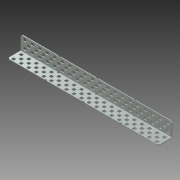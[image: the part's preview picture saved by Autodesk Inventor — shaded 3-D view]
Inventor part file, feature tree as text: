
AUTODESK INVENTOR PART (.ipt)
format: ipt  version: 2013 (Build 170138000, 138)  size: 1,454,592 bytes
history: native  units: in
note: dims shown in document units (in); Inventor stores cm internally (conversion verified against a paired STEP export)
features: other x127, extrude x118, sketch x10, pattern_linear x7, sheet_metal_op x4, projected_geometry x2, plane x1, mirror x1
ambient origin geometry x8: Origin, YZ Plane, XZ Plane, XY Plane, X Axis, Y Axis, Z Axis, Center Point
bodies: Solid1 (feature_tree)
feature tree (270):
  sheet_metal_op  "Face1"
  sheet_metal_op  "Flange1"
  sketch  "Sketch3"  dims[d2=0.032in]
  pattern_linear  "Rectangular Pattern1"  Spacing1=0.032in  [1 undecoded]
  pattern_linear  "Rectangular Pattern2"  Spacing1=0.032in  [1 undecoded]
  pattern_linear  "Rectangular Pattern3"  Spacing1=0.078in  [1 undecoded]
  pattern_linear  "Rectangular Pattern4"  Spacing1=0.182in  [1 undecoded]
  plane  "Work Plane1"
  mirror  "Mirror1"
  other  "Corner Chamfer1"
  pattern_linear  "Rectangular Pattern5"  Spacing1=0.182in  [1 undecoded]
  pattern_linear  "Rectangular Pattern6"  Spacing1=0.113in  [1 undecoded]
  pattern_linear  "Rectangular Pattern7"  Spacing1=0.159in  [1 undecoded]
  sketch  "Sketch1"  dims[d0=10.0in]
  other  "Plate1"
  sketch  "Sketch2"  dims[d1=0.922in]
  other  "Plate2"
  sheet_metal_op  "Bend1"
  sheet_metal_op  "Corner1"
  projected_geometry  "Projected Loop1"
  projected_geometry  "Projected Loop2"
  sketch  "Sketch4"  dims[d3=0.046in]
  sketch  "Sketch5"  dims[d4=0.023in]
  sketch  "Sketch6"  dims[d5=0.092in]
  other  "Srf1"
  other  "Srf2"
  other  "Srf3"
  other  "Srf4"
  other  "Srf5"
  other  "Srf6"
  other  "Srf7"
  other  "Srf8"
  other  "Srf9"
  other  "Srf10"
  other  "Srf11"
  other  "Srf12"
  other  "Srf13"
  other  "Srf14"
  other  "Srf15"
  other  "Srf16"
  other  "Srf17"
  other  "Srf18"
  other  "Srf19"
  other  "Srf20"
  other  "Srf21"
  other  "Srf22"
  other  "Srf23"
  other  "Srf24"
  other  "Srf25"
  other  "Srf26"
  other  "Srf27"
  other  "Srf28"
  other  "Srf29"
  other  "Srf30"
  other  "Srf31"
  other  "Srf32"
  other  "Srf33"
  other  "Srf34"
  other  "Srf35"
  other  "Srf36"
  other  "Srf37"
  other  "Srf38"
  other  "Srf39"
  other  "Srf40"
  sketch  "Sketch7"  dims[d6=0.032in]
  other  "Srf401"
  other  "Srf402"
  other  "Srf403"
  other  "Srf404"
  other  "Srf405"
  other  "Srf406"
  other  "Srf407"
  other  "Srf408"
  other  "Srf409"
  other  "Srf410"
  other  "Srf411"
  other  "Srf412"
  other  "Srf413"
  other  "Srf414"
  other  "Srf415"
  other  "Srf416"
  other  "Srf417"
  other  "Srf418"
  other  "Srf419"
  other  "Work Axis1"
  other  "Srf439"
  other  "Srf440"
  other  "Srf441"
  other  "Srf442"
  other  "Srf443"
  other  "Srf444"
  other  "Srf445"
  other  "Srf446"
  other  "Srf447"
  other  "Srf448"
  other  "Srf449"
  other  "Srf450"
  other  "Srf451"
  other  "Srf452"
  other  "Srf453"
  other  "Srf454"
  other  "Srf455"
  other  "Srf456"
  other  "Srf457"
  other  "Srf458"
  other  "Srf459"
  other  "Srf460"
  other  "Srf461"
  other  "Srf462"
  other  "Srf463"
  other  "Srf464"
  other  "Srf465"
  other  "Srf466"
  other  "Srf467"
  other  "Srf468"
  other  "Srf469"
  other  "Srf470"
  other  "Srf471"
  other  "Srf472"
  other  "Srf473"
  other  "Srf474"
  other  "Srf475"
  other  "Srf476"
  other  "Srf477"
  other  "Srf478"
  other  "Srf420"
  other  "Srf421"
  other  "Srf422"
  other  "Srf423"
  other  "Srf424"
  other  "Srf425"
  other  "Srf426"
  other  "Srf427"
  other  "Srf428"
  other  "Srf429"
  other  "Srf430"
  other  "Srf431"
  other  "Srf432"
  other  "Srf433"
  other  "Srf434"
  other  "Srf435"
  other  "Srf436"
  other  "Srf437"
  other  "Srf438"
  sketch  "Sketch8"  dims[d7=0.922in d8=90.0deg d9=0.032in]
  sketch  "Sketch9"  dims[d10=0.184in]
  sketch  "Sketch10"  dims[d11=0.046in d12=0.032in d13=0.032in d14=0.078in d15=0.182in d16=0.182in d17=0.113in d18=0.159in d19=0.02in d20=0.046in d21=0.0in d22=7.874in d24=0.5in d25=0.7874in d27=0.5in d28=0.182in d29=0.182in d30=0.25in d31=0.25in d32=0.046in d33=0.0in d34=0.02in d35=7.4803in d37=0.5in d38=1.0in d39=0.0in d40=7.874in d42=0.5in d43=0.7874in d45=0.5in d46=1.0in d47=0.0in d48=7.4803in d50=0.5in d51=135.0deg d52=0.0in d53=0.0in d54=0.0in d55=0.0in d56=0.0in d57=0.0in d58=0.0in d59=0.0in d60=0.0in d61=0.0in d62=0.0in d63=0.0in d64=0.0in d65=0.0in d66=0.0in d67=0.0in d68=0.0in d69=0.0in d70=0.0in d71=0.0in d72=0.0in d73=0.0in d74=0.0in d75=0.0in d76=0.0in d77=0.0in d78=0.0in d79=0.0in d80=0.0in d81=0.0in d82=0.0in d83=0.0in d84=0.0in d85=0.0in d86=0.0in d87=0.0in d88=0.0in d89=0.0in d90=0.0in d91=0.0in d92=0.0in d93=0.0in d94=0.0in d95=0.0in d96=0.0in d97=0.0in d98=0.0in d99=0.0in d100=0.0in d101=0.0in d102=0.0in d103=0.0in d104=0.0in d105=0.0in d106=0.0in d107=0.0in d108=0.0in d109=0.0in d110=0.0in d111=0.0in d112=0.0in d113=0.0in d114=0.0in d115=0.0in d116=0.0in d117=0.0in d118=0.0in d119=0.0in d120=0.0in d121=0.0in d122=0.0in d123=0.0in d124=0.0in d125=0.0in d126=0.0in d127=0.0in d128=0.0in d129=0.0in d130=0.0in d131=0.0in d132=0.0in d133=0.0in d134=0.0in d135=0.0in d136=0.0in d137=0.0in d138=0.0in d139=0.0in d140=0.0in d141=0.0in d142=0.0in d143=0.0in d144=0.0in d145=0.0in d146=0.0in d147=0.0in d148=0.0in d149=0.0in d150=0.0in d151=0.0in d152=0.0in d153=0.0in d154=0.0in d155=0.0in d156=0.0in d157=0.0in d158=0.0in d159=0.0in d160=0.0in d161=0.0in d162=0.0in d163=0.0in d164=0.0in d165=0.0in d166=0.0in d167=0.0in d168=0.0in d169=0.0in d170=0.09in d171=0.25in d172=45.0deg d173=0.16in d174=0.046in d175=0.0in d176=1.1811in d178=2.5in d179=0.16in d180=0.046in d181=0.0in d182=1.1811in d184=2.5in d186=0.078in d190=0.039in d191=0.6508in d192=0.046in d193=0.046in d194=0.0in d195=1.1811in d197=2.5in d198=0.0in d199=0.0in d200=0.0in d201=0.0in d202=0.0in d203=0.0in d204=0.0in d205=0.0in d206=0.0in d207=0.0in d208=0.0in d209=0.0in d210=0.0in d211=0.0in d212=0.0in d213=0.0in d214=0.0in d215=0.0in d216=0.0in d217=0.0in d218=0.0in d219=0.0in d220=0.0in d221=0.0in d222=0.0in d223=0.0in d224=0.0in d225=0.0in d226=0.0in d227=0.0in d228=0.0in d229=0.0in d230=0.0in d231=0.0in d232=0.0in d233=0.0in d234=0.0in d235=0.0in d236=0.0in d237=0.0in d238=0.0in d239=0.0in d240=0.0in d241=0.0in d242=0.0in d243=0.0in d244=0.0in d245=0.0in d246=0.0in d247=0.0in d248=0.0in d249=0.0in d250=0.0in d251=0.0in d252=0.0in d253=0.0in d254=0.0in d255=0.0in d256=0.0in d257=0.0in d258=0.0in d259=0.0in d260=0.0in d261=0.0in d262=0.0in d263=0.0in d264=0.0in d265=0.0in d266=0.0in d267=0.0in d268=0.0in d269=0.0in d270=0.0in d271=0.0in d272=0.0in d273=0.0in d274=0.0in d275=0.0in d276=0.0in d277=0.0in d278=0.0in d279=0.0in d280=0.0in d281=0.0in d282=0.0in d283=0.0in d284=0.0in d285=0.0in d286=0.0in d287=0.0in d288=0.0in d289=0.0in d290=0.0in d291=0.0in d292=0.0in d293=0.0in d294=0.0in d295=0.0in d296=0.0in d297=0.0in d298=0.0in d299=0.0in d300=0.0in d301=0.0in d302=0.0in d303=0.0in d304=0.0in d305=0.0in d306=0.0in d307=0.0in d308=0.0in d309=0.0in d310=0.0in d311=0.0in d312=0.0in d313=0.0in d314=0.0in d315=0.0in]
  other  "Cut1"
  other  "Cut2"
  extrude  "ExtrusionSrf1"  Depth=0.02in
  extrude  "ExtrusionSrf401"  Depth=0.046in
  other  "Cut3"
  other  "Cut4"
  other  "Cut5"
  extrude  "ExtrusionSrf2"  TaperAngle=0.0deg  [1 undecoded]
  extrude  "ExtrusionSrf3"  Depth=7.874in
  extrude  "ExtrusionSrf4"  Depth=0.7874in
  extrude  "ExtrusionSrf5"  Depth=0.182in
  extrude  "ExtrusionSrf6"  Depth=0.182in
  extrude  "ExtrusionSrf7"  Depth=0.25in
  extrude  "ExtrusionSrf8"  Depth=0.25in
  extrude  "ExtrusionSrf9"  Depth=0.046in
  extrude  "ExtrusionSrf10"  TaperAngle=0.0deg  [1 undecoded]
  extrude  "ExtrusionSrf11"  Depth=0.02in
  extrude  "ExtrusionSrf12"  Depth=7.4803in
  extrude  "ExtrusionSrf13"  Depth=1.0in TaperAngle=0.0deg
  extrude  "ExtrusionSrf14"  Depth=7.874in
  extrude  "ExtrusionSrf15"  Depth=1.0in TaperAngle=0.0deg
  extrude  "ExtrusionSrf16"  Depth=7.4803in
  extrude  "ExtrusionSrf17"  TaperAngle=135.0deg  [1 undecoded]
  extrude  "ExtrusionSrf18"  Depth=0.16in
  extrude  "ExtrusionSrf19"  Depth=0.046in
  extrude  "ExtrusionSrf20"  TaperAngle=0.0deg  [1 undecoded]
  extrude  "ExtrusionSrf21"  Depth=1.1811in
  extrude  "ExtrusionSrf22"  Depth=0.16in
  extrude  "ExtrusionSrf23"  Depth=0.046in
  extrude  "ExtrusionSrf24"  TaperAngle=0.0deg  [1 undecoded]
  extrude  "ExtrusionSrf25"  Depth=1.1811in
  extrude  "ExtrusionSrf26"  Depth=0.078in
  extrude  "ExtrusionSrf27"  Depth=0.039in
  extrude  "ExtrusionSrf28"  Depth=0.6508in
  extrude  "ExtrusionSrf29"  Depth=0.046in
  extrude  "ExtrusionSrf30"  Depth=0.046in
  extrude  "ExtrusionSrf31"  TaperAngle=0.0deg  [1 undecoded]
  extrude  "ExtrusionSrf32"  Depth=1.1811in
  extrude  "ExtrusionSrf33"  [1 undecoded]
  extrude  "ExtrusionSrf34"  [1 undecoded]
  extrude  "ExtrusionSrf35"  [1 undecoded]
  extrude  "ExtrusionSrf36"  [1 undecoded]
  extrude  "ExtrusionSrf37"  [1 undecoded]
  extrude  "ExtrusionSrf38"  [1 undecoded]
  extrude  "ExtrusionSrf39"  [1 undecoded]
  extrude  "ExtrusionSrf40"  [1 undecoded]
  extrude  "ExtrusionSrf402"  [1 undecoded]
  extrude  "ExtrusionSrf403"  [1 undecoded]
  extrude  "ExtrusionSrf404"  [1 undecoded]
  extrude  "ExtrusionSrf405"  [1 undecoded]
  extrude  "ExtrusionSrf406"  [1 undecoded]
  extrude  "ExtrusionSrf407"  [1 undecoded]
  extrude  "ExtrusionSrf408"  [1 undecoded]
  extrude  "ExtrusionSrf409"  [1 undecoded]
  extrude  "ExtrusionSrf410"  [1 undecoded]
  extrude  "ExtrusionSrf411"  [1 undecoded]
  extrude  "ExtrusionSrf412"  [1 undecoded]
  extrude  "ExtrusionSrf413"  [1 undecoded]
  extrude  "ExtrusionSrf414"  [1 undecoded]
  extrude  "ExtrusionSrf415"  [1 undecoded]
  extrude  "ExtrusionSrf416"  [1 undecoded]
  extrude  "ExtrusionSrf417"  [1 undecoded]
  extrude  "ExtrusionSrf418"  [1 undecoded]
  extrude  "ExtrusionSrf419"  [1 undecoded]
  extrude  "ExtrusionSrf420"  [1 undecoded]
  extrude  "ExtrusionSrf421"  [1 undecoded]
  extrude  "ExtrusionSrf422"  [1 undecoded]
  extrude  "ExtrusionSrf423"  [1 undecoded]
  extrude  "ExtrusionSrf424"  [1 undecoded]
  extrude  "ExtrusionSrf425"  [1 undecoded]
  extrude  "ExtrusionSrf426"  [1 undecoded]
  extrude  "ExtrusionSrf427"  [1 undecoded]
  extrude  "ExtrusionSrf428"  [1 undecoded]
  extrude  "ExtrusionSrf429"  [1 undecoded]
  extrude  "ExtrusionSrf430"  [1 undecoded]
  extrude  "ExtrusionSrf431"  [1 undecoded]
  extrude  "ExtrusionSrf432"  [1 undecoded]
  extrude  "ExtrusionSrf433"  [1 undecoded]
  extrude  "ExtrusionSrf434"  [1 undecoded]
  extrude  "ExtrusionSrf435"  [1 undecoded]
  extrude  "ExtrusionSrf436"  [1 undecoded]
  extrude  "ExtrusionSrf437"  [1 undecoded]
  extrude  "ExtrusionSrf438"  [1 undecoded]
  extrude  "ExtrusionSrf439"  [1 undecoded]
  extrude  "ExtrusionSrf440"  [1 undecoded]
  extrude  "ExtrusionSrf441"  [1 undecoded]
  extrude  "ExtrusionSrf442"  [1 undecoded]
  extrude  "ExtrusionSrf443"  [1 undecoded]
  extrude  "ExtrusionSrf444"  [1 undecoded]
  extrude  "ExtrusionSrf445"  [1 undecoded]
  extrude  "ExtrusionSrf446"  [1 undecoded]
  extrude  "ExtrusionSrf447"  [1 undecoded]
  extrude  "ExtrusionSrf448"  [1 undecoded]
  extrude  "ExtrusionSrf449"  [1 undecoded]
  extrude  "ExtrusionSrf450"  [1 undecoded]
  extrude  "ExtrusionSrf451"  [1 undecoded]
  extrude  "ExtrusionSrf452"  [1 undecoded]
  extrude  "ExtrusionSrf453"  [1 undecoded]
  extrude  "ExtrusionSrf454"  [1 undecoded]
  extrude  "ExtrusionSrf455"  [1 undecoded]
  extrude  "ExtrusionSrf456"  [1 undecoded]
  extrude  "ExtrusionSrf457"  [1 undecoded]
  extrude  "ExtrusionSrf458"  [1 undecoded]
  extrude  "ExtrusionSrf459"  [1 undecoded]
  extrude  "ExtrusionSrf460"  [1 undecoded]
  extrude  "ExtrusionSrf461"  [1 undecoded]
  extrude  "ExtrusionSrf462"  [1 undecoded]
  extrude  "ExtrusionSrf463"  [1 undecoded]
  extrude  "ExtrusionSrf464"  [1 undecoded]
  extrude  "ExtrusionSrf465"  [1 undecoded]
  extrude  "ExtrusionSrf466"  [1 undecoded]
  extrude  "ExtrusionSrf467"  [1 undecoded]
  extrude  "ExtrusionSrf468"  [1 undecoded]
  extrude  "ExtrusionSrf469"  [1 undecoded]
  extrude  "ExtrusionSrf470"  [1 undecoded]
  extrude  "ExtrusionSrf471"  [1 undecoded]
  extrude  "ExtrusionSrf472"  [1 undecoded]
  extrude  "ExtrusionSrf473"  [1 undecoded]
  extrude  "ExtrusionSrf474"  [1 undecoded]
  extrude  "ExtrusionSrf475"  [1 undecoded]
  extrude  "ExtrusionSrf476"  [1 undecoded]
  extrude  "ExtrusionSrf477"  [1 undecoded]
  extrude  "ExtrusionSrf478"  [1 undecoded]
note: 98 required parameter values undecoded (feature->parameter linkage not recoverable at this tier; creation-order binding heuristic only, values carry confidence <= 0.55)
